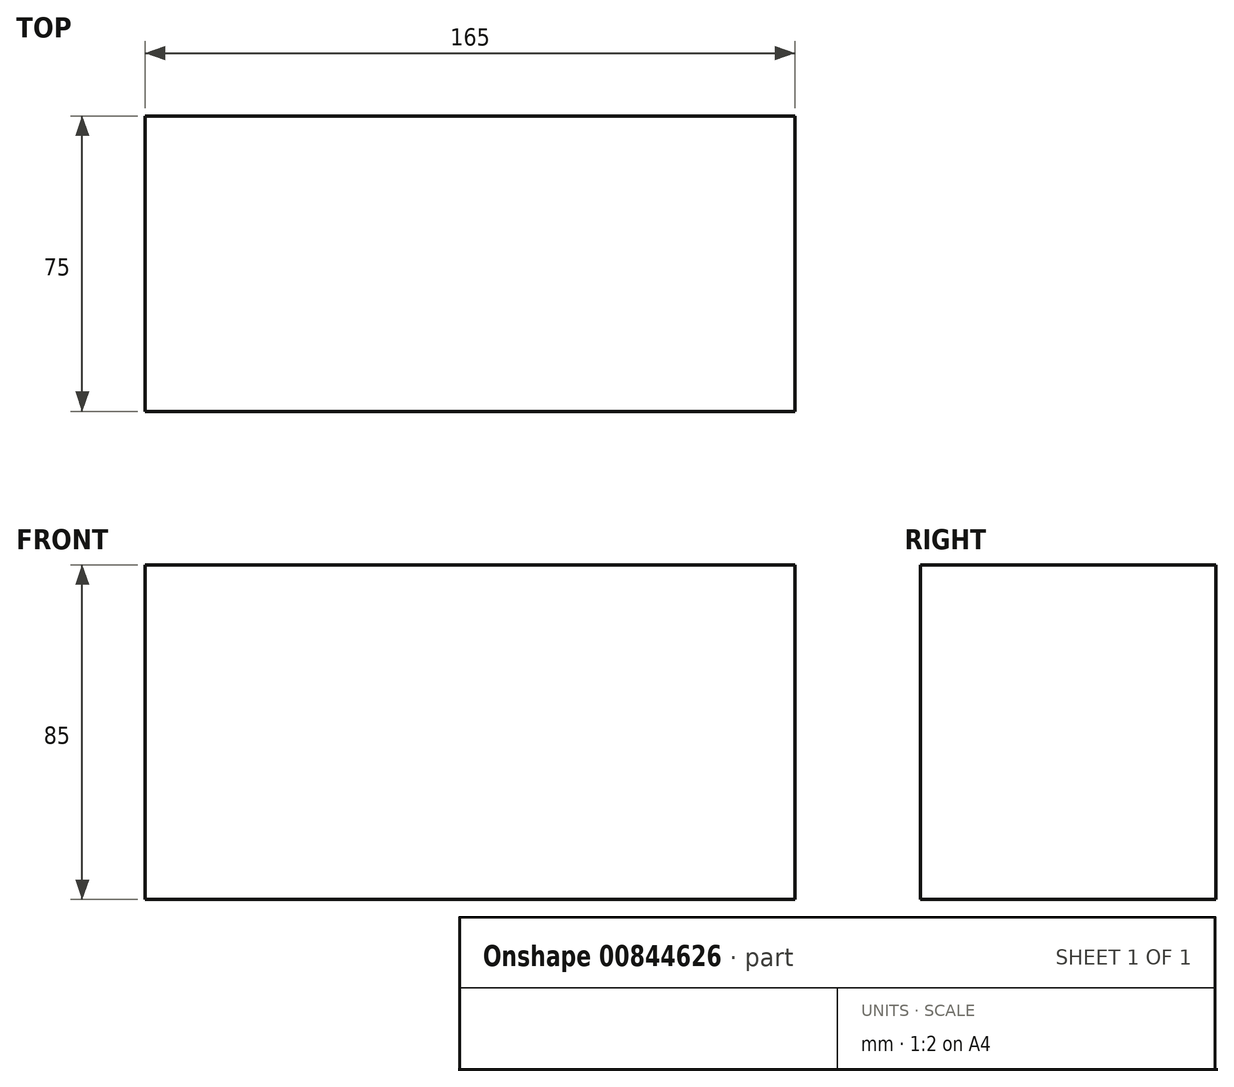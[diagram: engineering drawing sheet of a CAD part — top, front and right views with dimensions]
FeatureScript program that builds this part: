
annotation { "Feature Type Name" : "Feature", "Feature Type Description" : "" }
export const myFeature = defineFeature(function(context is Context, id is Id, definition is map)
    precondition{}
    {
        {
            var Q0;
            Q0=qCreatedBy(makeId("Front.planeOp"),FACE);
            var sketch = newSketch(context, id + "F0", { "sketchPlane" : qUnion([Q0])});
            skLineSegment(sketch, "E0.bottom", {"start": v(82.5, -42.5) * mm, "end": v(-82.5, -42.5) * mm});
            skLineSegment(sketch, "E0.top", {"start": v(82.5, 42.5) * mm, "end": v(-82.5, 42.5) * mm});
            skLineSegment(sketch, "E0.left", {"start": v(82.5, -42.5) * mm, "end": v(82.5, 42.5) * mm});
            skLineSegment(sketch, "E0.right", {"start": v(-82.5, -42.5) * mm, "end": v(-82.5, 42.5) * mm});
            skPoint(sketch, "E0.middle", {"position": v(0, 0) * mm});
            skSolve(sketch);
        }
        {
            var Q0;
            Q0=makeQuery(id+"F0.imprint","IMPRINT",FACE,{"disambiguationData":[TD([[makeQuery(id+"F0.imprint","IMPRINT",EDGE,{"derivedFrom":sQuery(id+"F0.wireOp",EDGE,"E0.bottom")}),-1.0]])]});
            extrude(context, id + "F1", {"entities" : qUnion([Q0]), "depth" : 75 * mm, "offsetDistance" : 25 * mm, "symmetric" : true});
        }
    });
